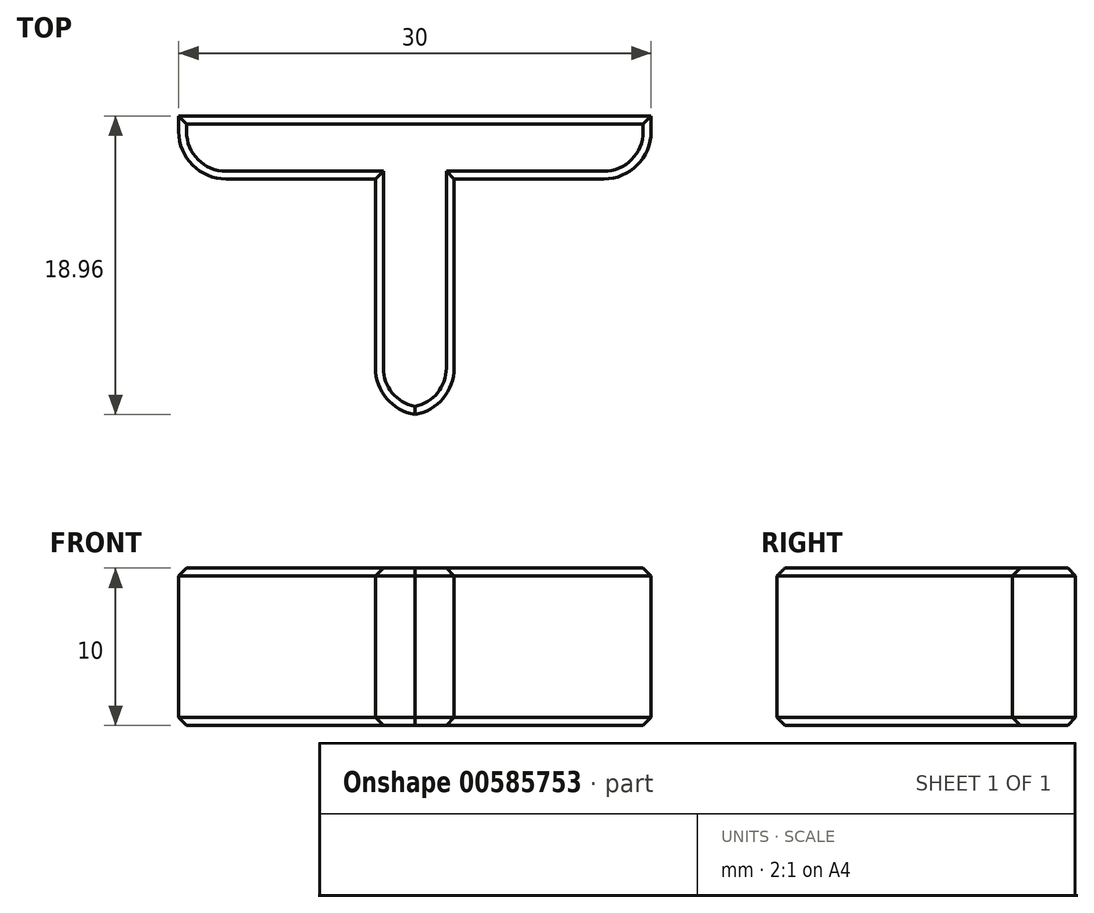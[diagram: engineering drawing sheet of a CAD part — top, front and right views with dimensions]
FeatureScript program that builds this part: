
annotation { "Feature Type Name" : "Feature", "Feature Type Description" : "" }
export const myFeature = defineFeature(function(context is Context, id is Id, definition is map)
    precondition{}
    {
        {
            var Q0;
            Q0=qCreatedBy(makeId("Top.planeOp"),FACE);
            var sketch = newSketch(context, id + "F0", { "sketchPlane" : qUnion([Q0])});
            skLineSegment(sketch, "E0", {"start": v(-15, 0) * mm, "end": v(-2.5, 0) * mm});
            skLineSegment(sketch, "E1", {"start": v(-2.5, 0) * mm, "end": v(-2.5, -15) * mm});
            skLineSegment(sketch, "E2", {"start": v(-2.5, -15) * mm, "end": v(2.5, -15) * mm});
            skLineSegment(sketch, "E3", {"start": v(2.5, -15) * mm, "end": v(2.5, 0) * mm});
            skLineSegment(sketch, "E4", {"start": v(2.5, 0) * mm, "end": v(15, 0) * mm});
            skLineSegment(sketch, "E5", {"start": v(15, 0) * mm, "end": v(15, 4) * mm});
            skLineSegment(sketch, "E6", {"start": v(15, 4) * mm, "end": v(-15, 4) * mm});
            skLineSegment(sketch, "E7", {"start": v(-15, 4) * mm, "end": v(-15, 0) * mm});
            skSolve(sketch);
        }
        {
            var Q0;
            Q0=makeQuery(id+"F0.imprint","IMPRINT",FACE,{"disambiguationData":[TD([[makeQuery(id+"F0.imprint","IMPRINT",EDGE,{"derivedFrom":sQuery(id+"F0.wireOp",EDGE,"E0")}),1.0]])]});
            extrude(context, id + "F1", {"entities" : qUnion([Q0]), "depth" : 10 * mm, "offsetDistance" : 25 * mm});
        }
        {
            var Q0;
            Q0=makeQuery(id+"F1.opExtrude","SWEPT_EDGE",EDGE,{"disambiguationData":[OSD([sQuery(id+"F0.wireOp",EDGE,"E1"),sQuery(id+"F0.wireOp",EDGE,"E2")])]});
            var Q1;
            Q1=makeQuery(id+"F1.opExtrude","SWEPT_EDGE",EDGE,{"disambiguationData":[OSD([sQuery(id+"F0.wireOp",EDGE,"E2"),sQuery(id+"F0.wireOp",EDGE,"E3")])]});
            var Q2;
            Q2=makeQuery(id+"F1.opExtrude","SWEPT_EDGE",EDGE,{"disambiguationData":[OSD([sQuery(id+"F0.wireOp",EDGE,"E0"),sQuery(id+"F0.wireOp",EDGE,"E7")])]});
            var Q3;
            Q3=makeQuery(id+"F1.opExtrude","SWEPT_EDGE",EDGE,{"disambiguationData":[OSD([sQuery(id+"F0.wireOp",EDGE,"E4"),sQuery(id+"F0.wireOp",EDGE,"E5")])]});
            fillet(context, id + "F2", {"entities" : qUnion([Q0, Q1, Q2, Q3]), "radius" : 3 * mm, "tangentPropagation" : true, "allowEdgeOverflow" : false});
        }
        {
            var Q0;
            Q0=makeQuery(id+"F1.opExtrude","CAP_FACE",FACE,{"disambiguationData":[OSD([sQuery(id+"F0.wireOp",EDGE,"E0"),sQuery(id+"F0.wireOp",EDGE,"E1"),sQuery(id+"F0.wireOp",EDGE,"E2"),sQuery(id+"F0.wireOp",EDGE,"E3"),sQuery(id+"F0.wireOp",EDGE,"E4"),sQuery(id+"F0.wireOp",EDGE,"E5"),sQuery(id+"F0.wireOp",EDGE,"E6"),sQuery(id+"F0.wireOp",EDGE,"E7")])],"isStart":false});
            var Q1;
            Q1=makeQuery(id+"F1.opExtrude","CAP_FACE",FACE,{"disambiguationData":[OSD([sQuery(id+"F0.wireOp",EDGE,"E0"),sQuery(id+"F0.wireOp",EDGE,"E1"),sQuery(id+"F0.wireOp",EDGE,"E2"),sQuery(id+"F0.wireOp",EDGE,"E3"),sQuery(id+"F0.wireOp",EDGE,"E4"),sQuery(id+"F0.wireOp",EDGE,"E5"),sQuery(id+"F0.wireOp",EDGE,"E6"),sQuery(id+"F0.wireOp",EDGE,"E7")])],"isStart":true});
            chamfer(context, id + "F3", {"entities" : qUnion([Q0, Q1]), "width" : .5 * mm, "tangentPropagation" : true});
        }
    });
